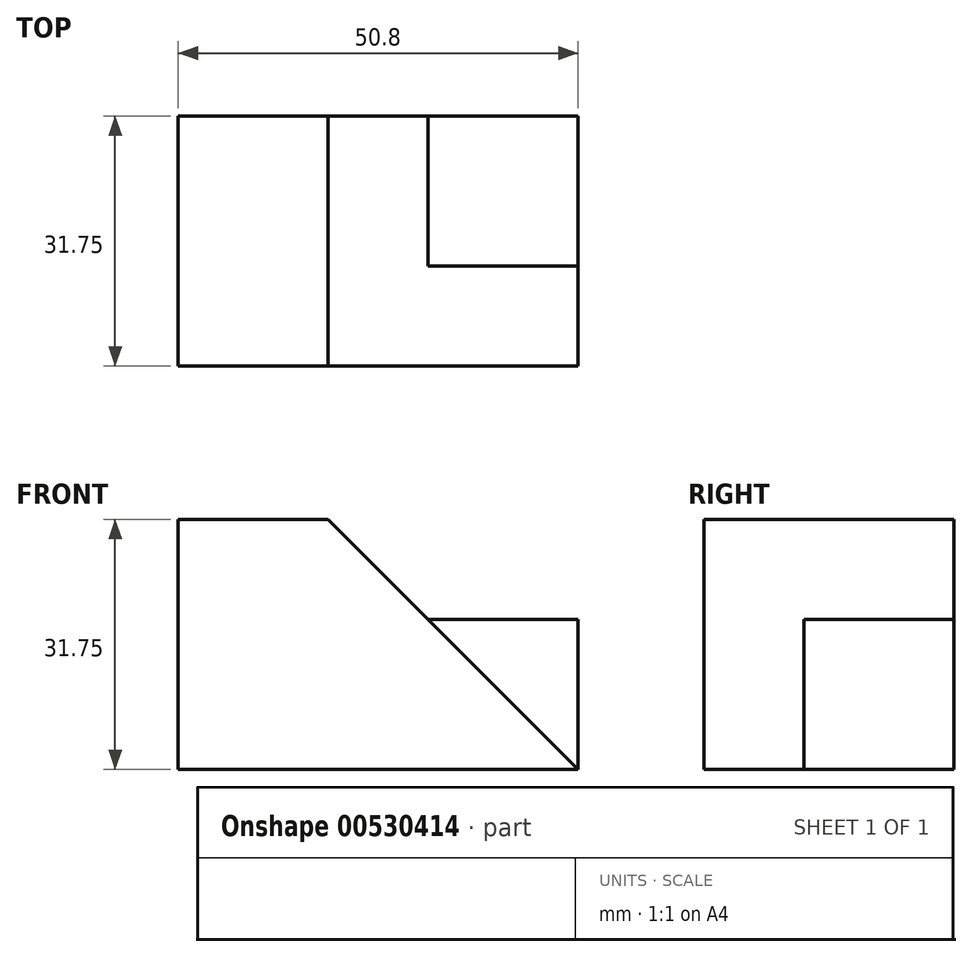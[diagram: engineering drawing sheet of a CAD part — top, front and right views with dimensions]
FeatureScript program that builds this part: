
annotation { "Feature Type Name" : "Feature", "Feature Type Description" : "" }
export const myFeature = defineFeature(function(context is Context, id is Id, definition is map)
    precondition{}
    {
        {
            var Q0;
            Q0=qCreatedBy(makeId("Front.planeOp"),FACE);
            var sketch = newSketch(context, id + "F0", { "sketchPlane" : qUnion([Q0])});
            skLineSegment(sketch, "E0", {"start": v(0, 31.75) * mm, "end": v(0, 0) * mm});
            skLineSegment(sketch, "E1", {"start": v(0, 31.75) * mm, "end": v(-50.8, 31.75) * mm});
            skLineSegment(sketch, "E2", {"start": v(-50.8, 31.75) * mm, "end": v(-50.8, 0) * mm});
            skLineSegment(sketch, "E3", {"start": v(-50.8, 0) * mm, "end": v(0, 0) * mm});
            skSolve(sketch);
        }
        {
            var Q0;
            Q0=makeQuery(id+"F0.imprint","IMPRINT",FACE,{"disambiguationData":[TD([[makeQuery(id+"F0.imprint","IMPRINT",EDGE,{"derivedFrom":sQuery(id+"F0.wireOp",EDGE,"E0")}),-1.0]])]});
            extrude(context, id + "F1", {"entities" : qUnion([Q0]), "depth" : 31.75 * mm, "offsetDistance" : 25.4 * mm});
        }
        {
            var Q0;
            Q0=makeQuery(id+"F1.opExtrude","CAP_FACE",FACE,{"disambiguationData":[OSD([sQuery(id+"F0.wireOp",EDGE,"E0"),sQuery(id+"F0.wireOp",EDGE,"E1"),sQuery(id+"F0.wireOp",EDGE,"E2"),sQuery(id+"F0.wireOp",EDGE,"E3")])],"isStart":false});
            var sketch = newSketch(context, id + "F2", { "sketchPlane" : qUnion([Q0])});
            skLineSegment(sketch, "E4", {"start": v(-31.75, 31.75) * mm, "end": v(0, 0) * mm});
            skSolve(sketch);
        }
        {
            var Q0;
            {var subQ0=sQuery(id+"F2.wireOp",EDGE,"E4");Q0=makeQuery(id+"F2.imprint","IMPRINT",FACE,{"disambiguationData":[TD([[makeQuery(id+"F2.imprint","IMPRINT",EDGE,{"derivedFrom":subQ0}),1.0]])]});}
            extrude(context, id + "F3", {"entities" : qUnion([Q0]), "operationType" : NewBodyOperationType.REMOVE, "oppositeDirection" : true, "depth" : 12.7 * mm, "offsetDistance" : 25.4 * mm});
        }
        {
            var Q0;
            Q0=makeQuery(id+"F3.boolean.opBoolean","COPY",FACE,{"derivedFrom":makeQuery(id+"F3.opExtrude","CAP_FACE",FACE,{"disambiguationData":[OSD([sQuery(id+"F0.wireOp",EDGE,"E0"),sQuery(id+"F0.wireOp",EDGE,"E1"),sQuery(id+"F2.wireOp",EDGE,"E4")])],"isStart":false})});
            var sketch = newSketch(context, id + "F4", { "sketchPlane" : qUnion([Q0])});
            skLineSegment(sketch, "E5", {"start": v(-19.05, 19.05) * mm, "end": v(0, 19.05) * mm});
            skSolve(sketch);
        }
        {
            var Q0;
            {var subQ0=sQuery(id+"F4.wireOp",EDGE,"E5");Q0=makeQuery(id+"F4.imprint","IMPRINT",FACE,{"disambiguationData":[TD([[makeQuery(id+"F4.imprint","IMPRINT",EDGE,{"derivedFrom":subQ0}),1.0]])]});}
            extrude(context, id + "F5", {"entities" : qUnion([Q0]), "operationType" : NewBodyOperationType.REMOVE, "endBound" : BoundingType.THROUGH_ALL, "oppositeDirection" : true, "depth" : 25.4 * mm, "offsetDistance" : 25.4 * mm});
        }
    });
